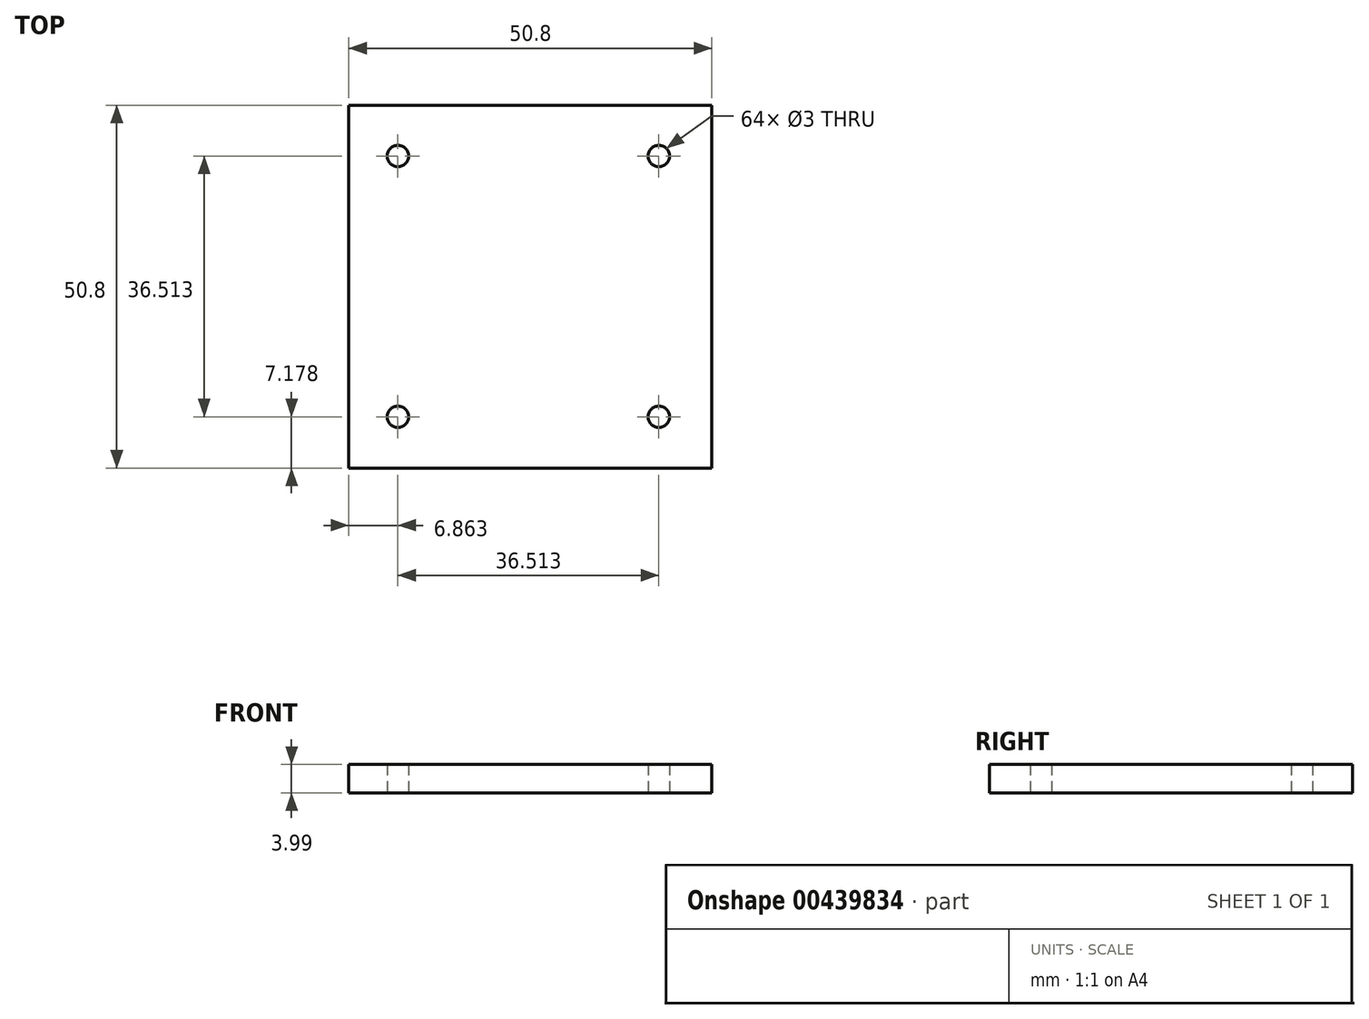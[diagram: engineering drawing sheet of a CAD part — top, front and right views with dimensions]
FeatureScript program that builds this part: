
annotation { "Feature Type Name" : "Feature", "Feature Type Description" : "" }
export const myFeature = defineFeature(function(context is Context, id is Id, definition is map)
    precondition{}
    {
        {
            var Q0;
            Q0=qCreatedBy(makeId("Top.planeOp"),FACE);
            var sketch = newSketch(context, id + "F0", { "sketchPlane" : qUnion([Q0])});
            skLineSegment(sketch, "E0.bottom", {"start": v(25.4, 25.4) * mm, "end": v(-25.4, 25.4) * mm});
            skLineSegment(sketch, "E0.top", {"start": v(25.4, -25.4) * mm, "end": v(-25.4, -25.4) * mm});
            skLineSegment(sketch, "E0.left", {"start": v(25.4, 25.4) * mm, "end": v(25.4, -25.4) * mm});
            skLineSegment(sketch, "E0.right", {"start": v(-25.4, 25.4) * mm, "end": v(-25.4, -25.4) * mm});
            skPoint(sketch, "E0.middle", {"position": v(0, 0) * mm});
            skPoint(sketch, "E1.middle", {"position": v(-0.28, 0.03) * mm});
            skCircle(sketch, "E2", {"center": v(17.98, 18.3) * mm, "radius": 1.5 * mm});
            skCircle(sketch, "E3", {"center": v(-18.54, 18.3) * mm, "radius": 1.5 * mm});
            skCircle(sketch, "E4", {"center": v(-18.54, -18.22) * mm, "radius": 1.5 * mm});
            skCircle(sketch, "E5", {"center": v(17.98, -18.22) * mm, "radius": 1.5 * mm});
            skSolve(sketch);
        }
        {
            var Q0;
            Q0=makeQuery(id+"F0.imprint","IMPRINT",FACE,{"disambiguationData":[TD([[makeQuery(id+"F0.imprint","IMPRINT",EDGE,{"derivedFrom":sQuery(id+"F0.wireOp",EDGE,"E0.bottom")}),1.0]])]});
            extrude(context, id + "F1", {"entities" : qUnion([Q0]), "depth" : 4 * mm});
        }
    });
